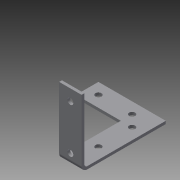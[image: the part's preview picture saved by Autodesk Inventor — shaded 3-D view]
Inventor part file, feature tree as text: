
AUTODESK INVENTOR PART (.ipt)
format: ipt  version: 2013 (Build 170138000, 138)  size: 126,976 bytes
history: native  units: in
note: dims shown in document units (in); Inventor stores cm internally (conversion verified against a paired STEP export)
features: sheet_metal_op x4, sketch x3, other x3
ambient origin geometry x8: Origin, YZ Plane, XZ Plane, XY Plane, X Axis, Y Axis, Z Axis, Center Point
bodies: Solid1 (feature_tree)
feature tree (10):
  sheet_metal_op  "Face1"
  sheet_metal_op  "Flange1"
  sketch  "Sketch1"  dims[d0=3.0in d1=1.0in d2=2.0in d3=2.0in d4=1.0in d5=0.266in d6=0.266in d7=0.266in d8=0.266in d9=0.5in d10=0.0in d11=0.5in d12=0.5in d13=0.5in d15=0.5in]
  other  "Plate1"
  sketch  "Sketch2"  dims[d17=0.75in]
  other  "Plate2"
  sheet_metal_op  "Bend1"
  sheet_metal_op  "Corner1"
  sketch  "Sketch3"  dims[d18=0.125in d19=0.125in d20=0.0625in d21=0.25in d22=0.125in d23=3.0in d24=90.0deg d25=0.125in d26=0.5in d27=0.125in d28=0.125in d29=0.266in d30=0.266in d31=0.5in d32=2.0in d33=0.125in d34=0.0in]
  other  "Cut1"
